FCSTD DOCUMENT  (FreeCAD 0.20R29177 (Git))
Label: FaceAV10Portrait
License: All rights reserved
LicenseURL: http://en.wikipedia.org/wiki/All_rights_reserved
objects: Sketcher::SketchObject×1, PartDesign::Body×1
note: 2 computed .brp shape members not serialized (recipe doc carries the construction recipe); baked Part::Feature solids carry a one-line shape summary decoded from their .brp
EXTERNAL_REF file=DonneesBoitier.FCStd obj=Spreadsheet

FEATURE [Sketcher::SketchObject] Sketch
  FullyConstrained = true
  MapMode = 5
  Support = -> [XY_Plane]
  expr: Constraints[100] = <<DonneesBoitier>>#<<Spreadsheet>>.xxFaEspaceHaut / 2
  expr: Constraints[103] = <<DonneesBoitier>>#<<Spreadsheet>>.xxRayonConge
  expr: Constraints[113] = <<DonneesBoitier>>#<<Spreadsheet>>.xxlargeur
  expr: Constraints[114] = <<DonneesBoitier>>#<<Spreadsheet>>.xxHauteur
  expr: Constraints[115] = <<DonneesBoitier>>#<<Spreadsheet>>.xxFaEspaceHaut
  expr: Constraints[116] = <<DonneesBoitier>>#<<Spreadsheet>>.xxFaEspaceHaut / 2
  expr: Constraints[117] = <<DonneesBoitier>>#<<Spreadsheet>>.xxAxeEncochesFaceAv
  expr: Constraints[119] = <<DonneesBoitier>>#<<Spreadsheet>>.xxAxeEncochesFaceAv
  expr: Constraints[11] = <<DonneesBoitier>>#Spreadsheet.xxLargeurEncasEcran
  expr: Constraints[12] = <<DonneesBoitier>>#Spreadsheet.xxHauteurEncasEcran
  expr: Constraints[13] = <<DonneesBoitier>>#Spreadsheet.xxDiametreTrou / 2
  expr: Constraints[16] = <<DonneesBoitier>>#<<Spreadsheet>>.xxDiametreTrou / 2
  expr: Constraints[18] = <<DonneesBoitier>>#Spreadsheet.xxHauteurEncasEcran / 2
  expr: Constraints[28] = <<DonneesBoitier>>#<<Spreadsheet>>.xxHautEncocheFemelle
  expr: Constraints[29] = <<DonneesBoitier>>#<<Spreadsheet>>.xxLargEncocheFemelle
  expr: Constraints[41] = <<DonneesBoitier>>#<<Spreadsheet>>.xxLargeurEncasEcran / 4 - <<DonneesBoitier>>#<<Spreadsheet>>.xxLargEconche / 2
  expr: Constraints[50] = <<DonneesBoitier>>#<<Spreadsheet>>.xxHautEncocheFemelle
  expr: Constraints[51] = <<DonneesBoitier>>#<<Spreadsheet>>.xxLargEncocheFemelle
  expr: Constraints[52] = <<DonneesBoitier>>#<<Spreadsheet>>.xxEspaceTrouEncoche
  expr: Constraints[95] = <<DonneesBoitier>>#<<Spreadsheet>>.xxEspaceTrouEncoche
  expr: Constraints[98] = <<DonneesBoitier>>#<<Spreadsheet>>.xxLargeurEncasEcran / 2
  sketch-geometry (66):
    g0: LineSegment StartX=110 StartY=10 StartZ=0 EndX=110 EndY=370 EndZ=0
    g1: LineSegment StartX=100 StartY=380 StartZ=0 EndX=-100 EndY=380 EndZ=0
    g2: LineSegment StartX=-110 StartY=370 StartZ=0 EndX=-110 EndY=10 EndZ=0
    g3: LineSegment StartX=-100 StartY=0 StartZ=0 EndX=100 EndY=0 EndZ=0
    g4: LineSegment StartX=-91 StartY=345 StartZ=0 EndX=91 EndY=345 EndZ=0
    g5: LineSegment StartX=91 StartY=345 StartZ=0 EndX=91 EndY=82 EndZ=0
    g6: LineSegment StartX=91 StartY=82 StartZ=0 EndX=-91 EndY=82 EndZ=0
    g7: LineSegment StartX=-91 StartY=82 StartZ=0 EndX=-91 EndY=345 EndZ=0
    g8: Circle CenterX=0 CenterY=362.5 CenterZ=0 NormalX=0 NormalY=0 NormalZ=1 AngleXU=0 Radius=2.625
    g9: Circle CenterX=0 CenterY=64.5 CenterZ=0 NormalX=0 NormalY=0 NormalZ=1 AngleXU=0 Radius=2.625
    g10: Circle CenterX=-100 CenterY=213.5 CenterZ=0 NormalX=0 NormalY=0 NormalZ=1 AngleXU=0 Radius=2.625
    g11: Circle CenterX=100 CenterY=213.5 CenterZ=0 NormalX=0 NormalY=0 NormalZ=1 AngleXU=0 Radius=2.625
    g12: LineSegment StartX=-53.2 StartY=365.1 StartZ=0 EndX=-38 EndY=365.1 EndZ=0
    g13: LineSegment StartX=-38 StartY=365.1 StartZ=0 EndX=-38 EndY=359.9 EndZ=0
    g14: LineSegment StartX=-38 StartY=359.9 StartZ=0 EndX=-53.2 EndY=359.9 EndZ=0
    g15: LineSegment StartX=-53.2 StartY=359.9 StartZ=0 EndX=-53.2 EndY=365.1 EndZ=0
    g16: LineSegment StartX=53.2 StartY=365.1 StartZ=0 EndX=38 EndY=365.1 EndZ=0
    g17: LineSegment StartX=38 StartY=365.1 StartZ=0 EndX=38 EndY=359.9 EndZ=0
    g18: LineSegment StartX=38 StartY=359.9 StartZ=0 EndX=53.2 EndY=359.9 EndZ=0
    g19: LineSegment StartX=53.2 StartY=359.9 StartZ=0 EndX=53.2 EndY=365.1 EndZ=0
    g20: LineSegment StartX=-102.6 StartY=243.7 StartZ=0 EndX=-97.4 EndY=243.7 EndZ=0
    g21: LineSegment StartX=-97.4 StartY=243.7 StartZ=0 EndX=-97.4 EndY=228.5 EndZ=0
    g22: LineSegment StartX=-97.4 StartY=228.5 StartZ=0 EndX=-102.6 EndY=228.5 EndZ=0
    g23: LineSegment StartX=-102.6 StartY=228.5 StartZ=0 EndX=-102.6 EndY=243.7 EndZ=0
    g24: LineSegment StartX=-100 StartY=213.5 StartZ=0 EndX=-100 EndY=243.7 EndZ=0
    g25: LineSegment StartX=-102.6 StartY=183.3 StartZ=0 EndX=-97.4 EndY=183.3 EndZ=0
    g26: LineSegment StartX=-97.4 StartY=183.3 StartZ=0 EndX=-97.4 EndY=198.5 EndZ=0
    g27: LineSegment StartX=-97.4 StartY=198.5 StartZ=0 EndX=-102.6 EndY=198.5 EndZ=0
    g28: LineSegment StartX=-102.6 StartY=198.5 StartZ=0 EndX=-102.6 EndY=183.3 EndZ=0
    g29: LineSegment StartX=-100 StartY=213.5 StartZ=0 EndX=-100 EndY=183.3 EndZ=0
    g30: LineSegment StartX=102.6 StartY=243.7 StartZ=0 EndX=97.4 EndY=243.7 EndZ=0
    g31: LineSegment StartX=97.4 StartY=243.7 StartZ=0 EndX=97.4 EndY=228.5 EndZ=0
    g32: LineSegment StartX=97.4 StartY=228.5 StartZ=0 EndX=102.6 EndY=228.5 EndZ=0
    g33: LineSegment StartX=102.6 StartY=228.5 StartZ=0 EndX=102.6 EndY=243.7 EndZ=0
    g34: LineSegment StartX=102.6 StartY=183.3 StartZ=0 EndX=97.4 EndY=183.3 EndZ=0
    g35: LineSegment StartX=97.4 StartY=183.3 StartZ=0 EndX=97.4 EndY=198.5 EndZ=0
    g36: LineSegment StartX=97.4 StartY=198.5 StartZ=0 EndX=102.6 EndY=198.5 EndZ=0
    g37: LineSegment StartX=102.6 StartY=198.5 StartZ=0 EndX=102.6 EndY=183.3 EndZ=0
    g38: LineSegment StartX=100 StartY=213.5 StartZ=0 EndX=100 EndY=183.3 EndZ=0
    g39: LineSegment StartX=100 StartY=213.5 StartZ=0 EndX=100 EndY=243.7 EndZ=0
    g40: ArcOfCircle CenterX=-100 CenterY=10 CenterZ=0 NormalX=0 NormalY=0 NormalZ=1 AngleXU=0 Radius=10 StartAngle=3.14159 EndAngle=4.71239
    g41: ArcOfCircle CenterX=-100 CenterY=370 CenterZ=0 NormalX=0 NormalY=0 NormalZ=1 AngleXU=0 Radius=10 StartAngle=1.5708 EndAngle=3.14159
    g42: ArcOfCircle CenterX=100 CenterY=370 CenterZ=0 NormalX=0 NormalY=0 NormalZ=1 AngleXU=0 Radius=10 StartAngle=-9e-16 EndAngle=1.5708
    g43: ArcOfCircle CenterX=100 CenterY=10 CenterZ=0 NormalX=0 NormalY=0 NormalZ=1 AngleXU=0 Radius=10 StartAngle=4.71239 EndAngle=6.28319
    g44: Circle CenterX=-100 CenterY=64.5 CenterZ=0 NormalX=0 NormalY=0 NormalZ=1 AngleXU=0 Radius=2.625
    g45: LineSegment StartX=-102.6 StartY=94.7 StartZ=0 EndX=-97.4 EndY=94.7 EndZ=0
    g46: LineSegment StartX=-97.4 StartY=94.7 StartZ=0 EndX=-97.4 EndY=79.5 EndZ=0
    g47: LineSegment StartX=-97.4 StartY=79.5 StartZ=0 EndX=-102.6 EndY=79.5 EndZ=0
    g48: LineSegment StartX=-102.6 StartY=79.5 StartZ=0 EndX=-102.6 EndY=94.7 EndZ=0
    g49: LineSegment StartX=-100 StartY=64.5 StartZ=0 EndX=-100 EndY=94.7 EndZ=0
    g50: LineSegment StartX=-102.6 StartY=34.3 StartZ=0 EndX=-97.4 EndY=34.3 EndZ=0
    g51: LineSegment StartX=-97.4 StartY=34.3 StartZ=0 EndX=-97.4 EndY=49.5 EndZ=0
    g52: LineSegment StartX=-97.4 StartY=49.5 StartZ=0 EndX=-102.6 EndY=49.5 EndZ=0
    g53: LineSegment StartX=-102.6 StartY=49.5 StartZ=0 EndX=-102.6 EndY=34.3 EndZ=0
    g54: LineSegment StartX=-100 StartY=64.5 StartZ=0 EndX=-100 EndY=34.3 EndZ=0
    g55: Circle CenterX=100 CenterY=64.5 CenterZ=0 NormalX=0 NormalY=0 NormalZ=1 AngleXU=0 Radius=2.625
    g56: LineSegment StartX=97.4 StartY=94.7 StartZ=0 EndX=102.6 EndY=94.7 EndZ=0
    g57: LineSegment StartX=102.6 StartY=94.7 StartZ=0 EndX=102.6 EndY=79.5 EndZ=0
    g58: LineSegment StartX=102.6 StartY=79.5 StartZ=0 EndX=97.4 EndY=79.5 EndZ=0
    g59: LineSegment StartX=97.4 StartY=79.5 StartZ=0 EndX=97.4 EndY=94.7 EndZ=0
    g60: LineSegment StartX=100 StartY=64.5 StartZ=0 EndX=100 EndY=94.7 EndZ=0
    g61: LineSegment StartX=97.4 StartY=34.3 StartZ=0 EndX=102.6 EndY=34.3 EndZ=0
    g62: LineSegment StartX=102.6 StartY=34.3 StartZ=0 EndX=102.6 EndY=49.5 EndZ=0
    g63: LineSegment StartX=102.6 StartY=49.5 StartZ=0 EndX=97.4 EndY=49.5 EndZ=0
    g64: LineSegment StartX=97.4 StartY=49.5 StartZ=0 EndX=97.4 EndY=34.3 EndZ=0
    g65: LineSegment StartX=100 StartY=64.5 StartZ=0 EndX=100 EndY=34.3 EndZ=0
  constraints (181):
    c: Horizontal(g1)
    c: Horizontal(g3)
    c: Vertical(g0)
    c: Vertical(g2)
    c: Coincident(g4,g5)
    c: Coincident(g5,g6)
    c: Coincident(g6,g7)
    c: Coincident(g7,g4)
    c: Horizontal(g6)
    c: Vertical(g5)
    c: Vertical(g7)
    c: DistanceX(g4,g4) = 182
    c: DistanceY(g5,g5) = 263
    c: Radius(g9) = 2.625
    c: PointOnObject(g9,g-2)
    c: Equal(g9,g10) = 5
    c: Radius(g8) = 2.625
    c: Equal(g10,g11)
    c: DistanceY(g11,g4) = 131.5
    c: PointOnObject(g8,g-2)
    c: Coincident(g12,g13)
    c: Coincident(g13,g14)
    c: Coincident(g14,g15)
    c: Coincident(g15,g12)
    c: Horizontal(g12)
    c: Horizontal(g14)
    c: Vertical(g13)
    c: Vertical(g15)
    c: DistanceY(g14,g12) = 5.2
    c: DistanceX(g12,g12) = 15.2
    c: Coincident(g16,g17)
    c: Coincident(g17,g18)
    c: Coincident(g18,g19)
    c: Coincident(g19,g16)
    c: Horizontal(g16)
    c: Horizontal(g18)
    c: Vertical(g17)
    c: Vertical(g19)
    c: Equal(g12,g16)
    c: Equal(g13,g17)
    c: Symmetric(g12,g16,g-2)
    c: DistanceX(g12,g-1) = 38
    c: Coincident(g20,g21)
    c: Coincident(g21,g22)
    c: Coincident(g22,g23)
    c: Coincident(g23,g20)
    c: Horizontal(g20)
    c: Horizontal(g22)
    c: Vertical(g21)
    c: Vertical(g23)
    c: DistanceX(g20,g20) = 5.2
    c: DistanceY(g21,g20) = 15.2
    c: DistanceY(g10,g22) = 15
    c: Coincident(g24,g10)
    c: Vertical(g24)
    c: Symmetric(g20,g20,g24)
    c: Coincident(g25,g26)
    c: Coincident(g26,g27)
    c: Coincident(g27,g28)
    c: Coincident(g28,g25)
    c: Horizontal(g25)
    c: Horizontal(g27)
    c: Vertical(g26)
    c: Vertical(g28)
    c: Equal(g21,g28)
    c: Coincident(g29,g10)
    c: PointOnObject(g29,g25)
    c: Symmetric(g26,g27,g29)
    c: Symmetric(g21,g27,g10)
    c: Coincident(g30,g31)
    c: Coincident(g31,g32)
    c: Coincident(g32,g33)
    c: Coincident(g33,g30)
    c: Horizontal(g30)
    c: Horizontal(g32)
    c: Vertical(g31)
    c: Coincident(g34,g35)
    c: Coincident(g35,g36)
    c: Coincident(g36,g37)
    c: Coincident(g37,g34)
    c: Horizontal(g34)
    c: Horizontal(g36)
    c: Vertical(g35)
    c: Equal(g31,g37)
    c: Coincident(g38,g11)
    c: PointOnObject(g38,g34)
    c: Coincident(g39,g11)
    c: PointOnObject(g39,g30)
    c: Equal(g32,g30)
    c: Equal(g30,g36)
    c: Equal(g34,g22)
    c: Equal(g33,g21)
    c: Equal(g35,g37)
    c: Symmetric(g31,g32,g39)
    c: Symmetric(g35,g36,g38)
    c: DistanceY(g11,g32) = 15
    c: DistanceY(g35,g11) = 15
    c: Horizontal(g4)
    c: DistanceX(g4,g8) = 91
    c: DistanceY(g8,g12) = 2.6
    c: DistanceY(g9,g5) = 17.5
    c: Tangent(g2,g40) = -1.5708
    c: Tangent(g3,g40) = -1.5708
    c: Radius(g40) = 10
    c: Tangent(g1,g41) = -1.5708
    c: Tangent(g2,g41) = -1.5708
    c: Tangent(g1,g42) = -1.5708
    c: Tangent(g0,g42) = -1.5708
    c: Tangent(g0,g43) = -1.5708
    c: Tangent(g3,g43) = -1.5708
    c: Equal(g41,g42)
    c: Equal(g42,g43)
    c: Equal(g43,g40)
    c: DistanceX(g2,g0) = 220
    c: DistanceY(g3,g1) = 380
    c: DistanceY(g4,g1) = 35
    c: DistanceY(g8,g1) = 17.5
    c: DistanceX(g2,g10) = 10
    c: Symmetric(g10,g11,g-2)
    c: DistanceX(g11,g0) = 10
    c: PointOnObject(g-1,g3)
    c: Coincident(g45,g46)
    c: Coincident(g46,g47)
    c: Coincident(g47,g48)
    c: Coincident(g48,g45)
    c: Horizontal(g45)
    c: Horizontal(g47)
    c: Vertical(g46)
    c: Vertical(g48)
    c: Equal(g20,g45) = 5.2
    c: DistanceY(g46,g45) = 15.2
    c: DistanceY(g44,g47) = 15
    c: Coincident(g49,g44)
    c: Vertical(g49)
    c: Symmetric(g45,g45,g49)
    c: Coincident(g50,g51)
    c: Coincident(g51,g52)
    c: Coincident(g52,g53)
    c: Coincident(g53,g50)
    c: Horizontal(g50)
    c: Horizontal(g52)
    c: Vertical(g51)
    c: Vertical(g53)
    c: Equal(g46,g53)
    c: Coincident(g54,g44)
    c: PointOnObject(g54,g50)
    c: Symmetric(g51,g52,g54)
    c: Symmetric(g46,g52,g44)
    c: DistanceX(g10,g44) = 0
    c: DistanceY(g44,g9) = 0
    c: Equal(g44,g10)
    c: Coincident(g56,g57)
    c: Coincident(g57,g58)
    c: Coincident(g58,g59)
    c: Coincident(g59,g56)
    c: Horizontal(g56)
    c: Horizontal(g58)
    c: Vertical(g57)
    c: Vertical(g59)
    c: DistanceY(g57,g56) = 15.2
    c: DistanceY(g55,g58) = 15
    c: Coincident(g60,g55)
    c: Vertical(g60)
    c: Symmetric(g56,g56,g60)
    c: Coincident(g61,g62)
    c: Coincident(g62,g63)
    c: Coincident(g63,g64)
    c: Coincident(g64,g61)
    c: Horizontal(g61)
    c: Horizontal(g63)
    c: Vertical(g62)
    c: Vertical(g64)
    c: Equal(g57,g64)
    c: Coincident(g65,g55)
    c: PointOnObject(g65,g61)
    c: Symmetric(g62,g63,g65)
    c: Symmetric(g57,g63,g55)
    c: DistanceY(g55,g9) = 0
    c: DistanceX(g11,g55) = 0
    c: Equal(g55,g9)
    c: Equal(g56,g47)
FEATURE [PartDesign::Body] Body  label="Body-faceAv"
  Group = -> [Sketch]
  Origin = -> Origin
